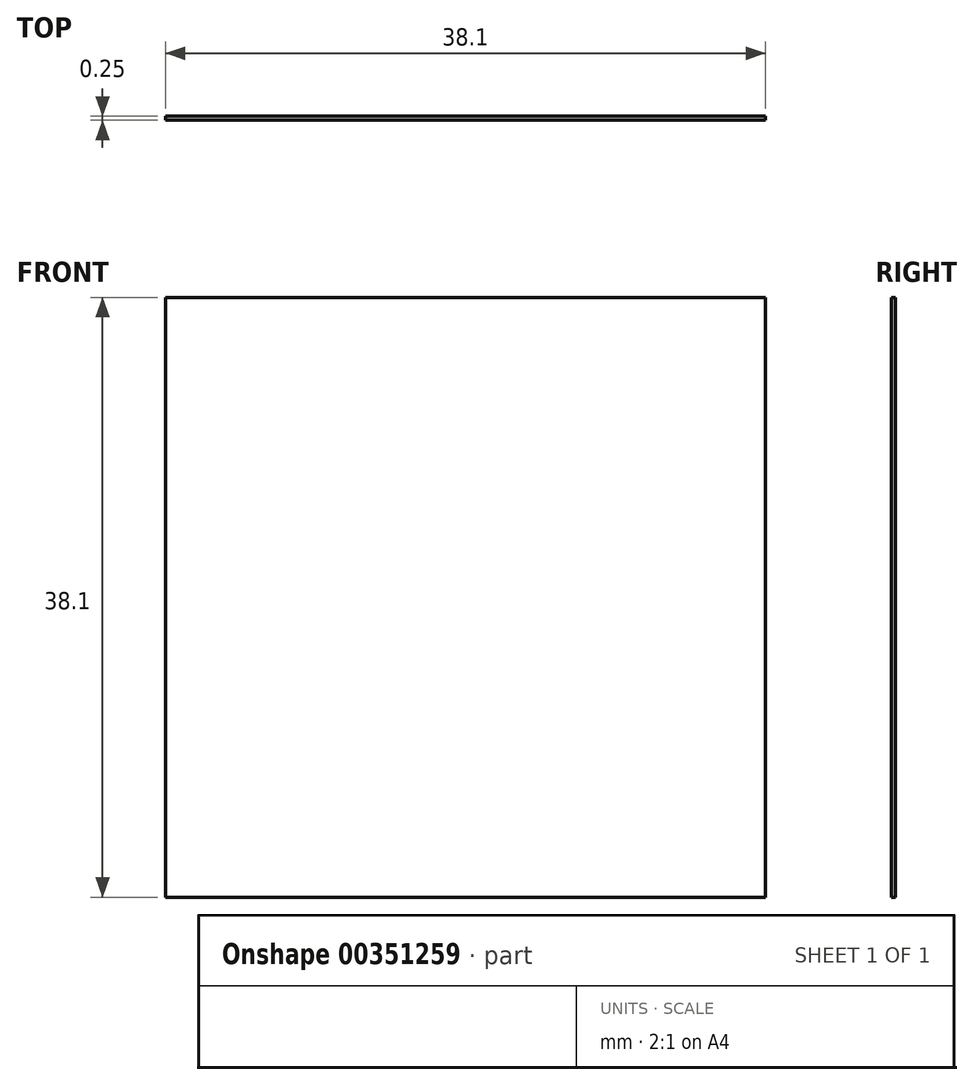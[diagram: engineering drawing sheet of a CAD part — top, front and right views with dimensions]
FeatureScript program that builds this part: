
annotation { "Feature Type Name" : "Feature", "Feature Type Description" : "" }
export const myFeature = defineFeature(function(context is Context, id is Id, definition is map)
    precondition{}
    {
        {
            var Q0;
            Q0=qCreatedBy(makeId("Front.planeOp"),FACE);
            var sketch = newSketch(context, id + "F0", { "sketchPlane" : qUnion([Q0])});
            skCircle(sketch, "E0.cCircle", {"center": v(-0.06, 0) * mm, "radius": 19.05 * mm});
            skLineSegment(sketch, "E0.0", {"start": v(19, 19.05) * mm, "end": v(19, -19.05) * mm});
            skLineSegment(sketch, "E0.1", {"start": v(19, -19.05) * mm, "end": v(-19.1, -19.05) * mm});
            skLineSegment(sketch, "E0.2", {"start": v(-19.1, -19.05) * mm, "end": v(-19.1, 19.05) * mm});
            skLineSegment(sketch, "E0.3", {"start": v(-19.1, 19.05) * mm, "end": v(19, 19.05) * mm});
            skPoint(sketch, "E0.0.midPoint", {"position": v(19, 0) * mm});
            skSolve(sketch);
        }
        {
            var Q0;
            Q0 = qSketchRegion(id + "F0", true);
            extrude(context, id + "F1", {"entities" : qUnion([Q0]), "depth" : 0.25 * mm});
        }
    });
